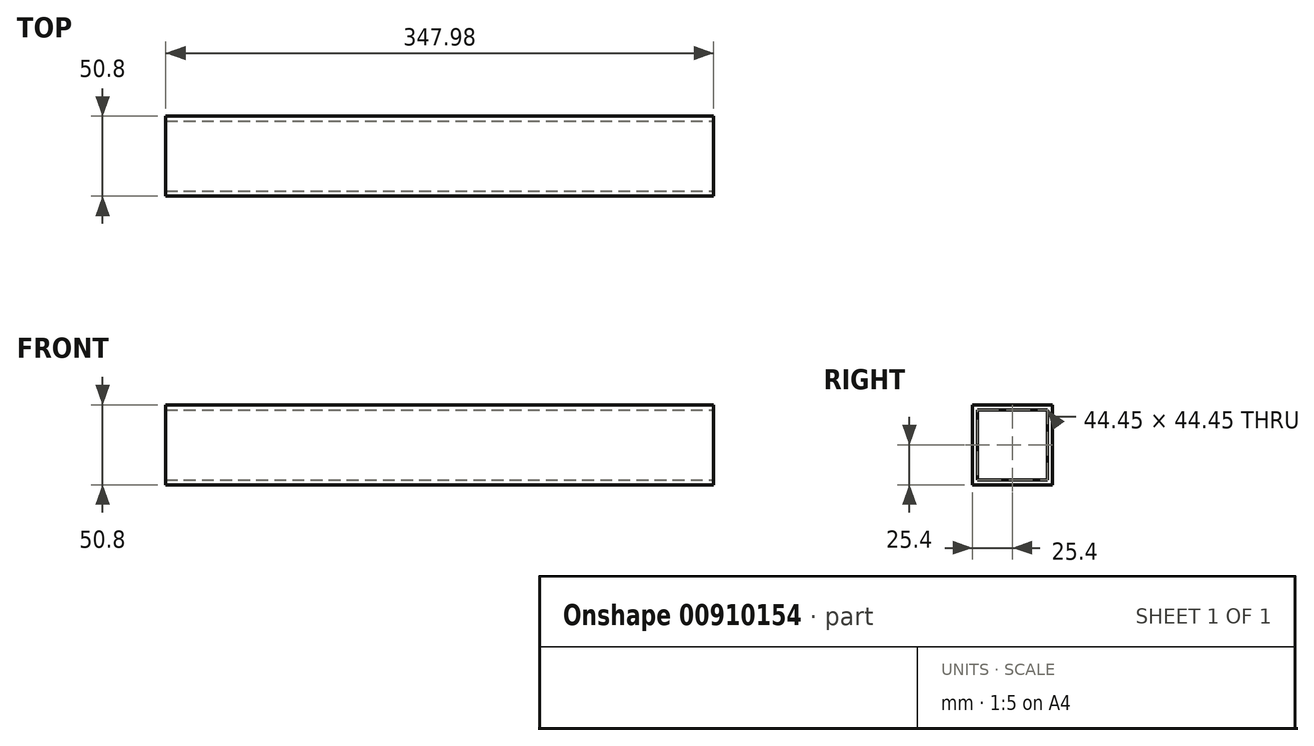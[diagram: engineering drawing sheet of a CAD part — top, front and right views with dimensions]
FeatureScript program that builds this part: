
annotation { "Feature Type Name" : "Feature", "Feature Type Description" : "" }
export const myFeature = defineFeature(function(context is Context, id is Id, definition is map)
    precondition{}
    {
        {
            var Q0;
            Q0=qCreatedBy(makeId("Front.planeOp"),FACE);
            var sketch = newSketch(context, id + "F0", { "sketchPlane" : qUnion([Q0])});
            skLineSegment(sketch, "E0.bottom", {"start": v(-174, 25.4) * mm, "end": v(174, 25.4) * mm});
            skLineSegment(sketch, "E0.top", {"start": v(-174, -25.4) * mm, "end": v(174, -25.4) * mm});
            skLineSegment(sketch, "E0.left", {"start": v(-174, 25.4) * mm, "end": v(-174, -25.4) * mm});
            skLineSegment(sketch, "E0.right", {"start": v(174, 25.4) * mm, "end": v(174, -25.4) * mm});
            skPoint(sketch, "E0.middle", {"position": v(0, 0) * mm});
            skSolve(sketch);
        }
        {
            var Q0;
            Q0 = qSketchRegion(id + "F0", true);
            extrude(context, id + "F1", {"entities" : qUnion([Q0]), "endBound" : BoundingType.SYMMETRIC, "depth" : 50.8 * mm, "offsetDistance" : 25.4 * mm});
        }
        {
            var Q0;
            Q0=makeQuery(id+"F1.opExtrude","SWEPT_FACE",FACE,{"disambiguationData":[OSD([sQuery(id+"F0.wireOp",EDGE,"E0.left")])]});
            var Q1;
            Q1=makeQuery(id+"F1.opExtrude","SWEPT_FACE",FACE,{"disambiguationData":[OSD([sQuery(id+"F0.wireOp",EDGE,"E0.right")])]});
            shell(context, id + "F2", {"entities" : qUnion([Q0, Q1]), "thickness" : 3.17 * mm});
        }
    });
